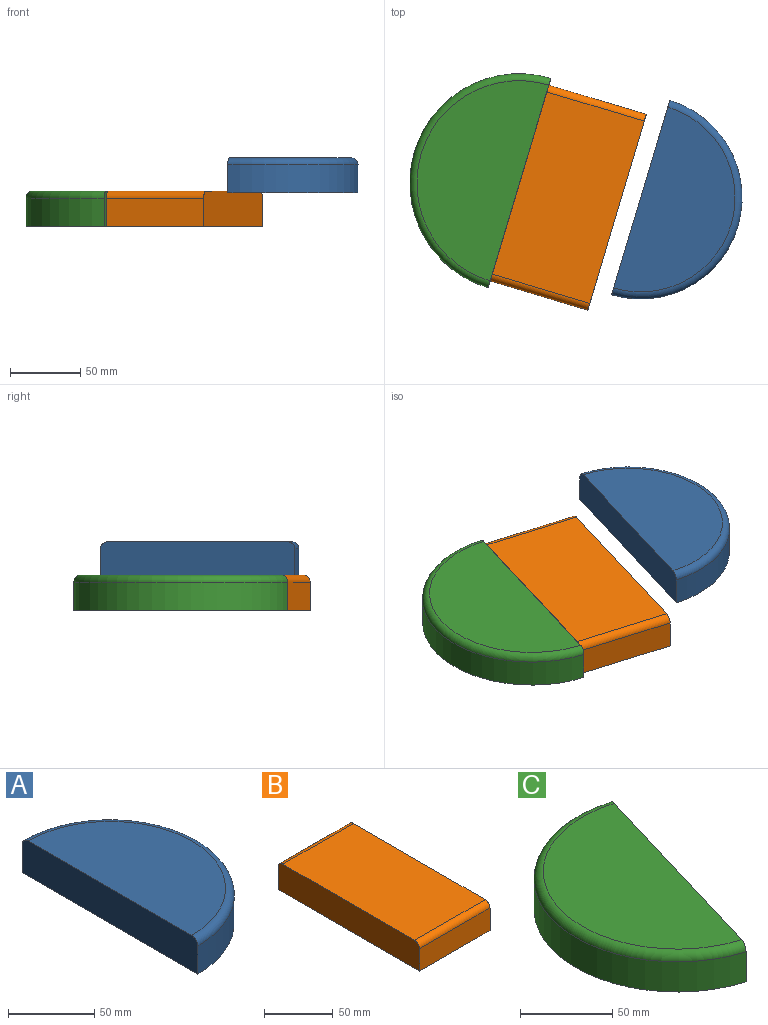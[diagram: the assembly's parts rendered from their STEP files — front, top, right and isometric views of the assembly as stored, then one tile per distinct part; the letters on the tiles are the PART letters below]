
ASSEMBLY  parts=3 mates=2
PART A: 5 faces, bbox 78.2x156.5x25 mm
  f0: plane 144.54x25mm, normal (-1,0,0), area 3602.9mm2, adj f1,f2,f3,f4
  f1: cylinder r=72.27mm len=144.54mm, axis (0,0,-1), area 4541mm2, adj f0,f3,f4
  f2: plane 134.54x67.27mm, normal (0,0,1), area 7108.7mm2, adj f0,f4
  f3: plane 144.54x72.27mm, normal (0,0,-1), area 8204.6mm2, adj f0,f1
  f4: torus R=67.27mm, axis (0,0,1), area 1738.4mm2, adj f0,f1,f2
PART B: 8 faces, bbox 72.5x145.6x25 mm
  f0: plane 72.5x20mm, normal (0,-1,0), area 1449.9mm2, adj f1,f3,f5,f7
  f1: plane 145.56x25mm, normal (1,0,0), area 3628.3mm2, adj f0,f2,f4,f5,f6,f7
  f2: plane 72.5x20mm, normal (0,1,0), area 1449.9mm2, adj f1,f3,f5,f6
  f3: plane 145.56x25mm, normal (-1,0,0), area 3628.3mm2, adj f0,f2,f4,f5,f6,f7
  f4: plane 135.56x72.5mm, normal (0,0,1), area 9827.7mm2, adj f1,f3,f6,f7
  f5: plane 145.56x72.5mm, normal (0,0,-1), area 10552.7mm2, adj f0,f1,f2,f3
  f6: cylinder r=5mm len=72.5mm, axis (1,0,0), area 569.4mm2, adj f1,f2,f3,f4
  f7: cylinder r=5mm len=72.5mm, axis (-1,0,0), area 569.4mm2, adj f0,f1,f3,f4
PART C: 5 faces, bbox 108.8x165.1x25 mm
  f0: cylinder r=77.84mm len=152.51mm, axis (0,0,-1), area 4904.2mm2, adj f1,f3,f4
  f1: plane 149.17x44.64mm, normal (0.96,-0.29,0), area 3881.4mm2, adj f0,f2,f3,f4
  f2: plane 142.72x94.04mm, normal (0,0,1), area 8382.7mm2, adj f1,f4
  f3: plane 152.51x100.47mm, normal (0,0,-1), area 9569.5mm2, adj f0,f1
  f4: torus R=72.84mm, axis (0,0,1), area 1881.1mm2, adj f0,f1,f2
PLACE A rot(axis=(0,0,-1),16.7deg) t=(-1.12,-2.71,1.86)mm
PLACE B rot(axis=(0,0,-1),16.7deg) t=(95.71,-58.18,-21.72)mm
PLACE C t=(301.73,-129.75,-21.73)mm
MATE parallel B.f3 <-> C.f1  axis (-0.96,0.29,0) through (-89.57,0.73,-9.26)mm
MATE parallel A.f0 <-> B.f1  axis (-0.96,0.29,0) through (-3.2,-9.66,14.33)mm
